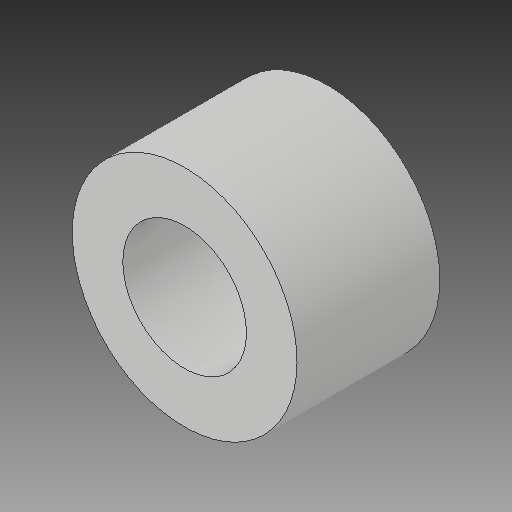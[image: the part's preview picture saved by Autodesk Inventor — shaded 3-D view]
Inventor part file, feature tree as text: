
AUTODESK INVENTOR PART (.ipt)
format: ipt  version: 2018 (Build 220112000, 112)  size: 101,376 bytes
history: native  units: mm
features: other x4, extrude x1, sketch x1, reference x1
ambient origin geometry x8: Origin, YZ Plane, XZ Plane, XY Plane, X Axis, Y Axis, Z Axis, Center Point
bodies: Solid1 (feature_tree)
feature tree (7):
  extrude  "Extrusion1"  Depth=10.0mm
  sketch  "Sketch1"  dims[d0=5.5mm d1=10.0mm d2=6.35mm d3=0.0mm]
  reference  "Reference1"
  parser-record x1  (decoder bookkeeping rows leaked as tree rows — omitted from the tree; the rows remain in map.json)
  other  "DelrinY-Wheel-Top.iam"
  other  "Delrin Wheel:1"
  other  "SKF 625:1"
note: 1 file-system path scrubbed to <path> (originals preserved in map.json)
